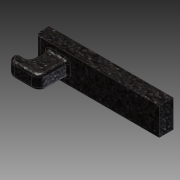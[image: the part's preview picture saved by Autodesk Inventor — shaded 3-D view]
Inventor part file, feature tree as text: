
AUTODESK INVENTOR PART (.ipt)
format: ipt  version: 2012 (Build 160160000, 160)  size: 162,304 bytes
history: native  units: mm
features: fillet x10, extrude x2, sketch x1
ambient origin geometry x8: Origin, YZ Plane, XZ Plane, XY Plane, X Axis, Y Axis, Z Axis, Center Point
bodies: Solid1 (feature_tree)
feature tree (13):
  sketch  "Sketch1"  dims[d0=13.0mm d1=4.0mm d2=8.0mm d3=7.3mm d4=49.5mm d5=5.6mm d6=5.6mm d7=0.0mm d8=3.0mm d9=2.0mm d10=2.0mm d11=3.0mm d12=1.0mm d13=2.0mm d14=1.0mm d15=1.0mm d16=1.0mm d17=11.0mm d18=0.0mm d19=2.0mm]
  extrude  "Extrusion1"  Depth=4.0mm
  extrude  "Extrusion2"  Depth=8.0mm
  fillet  "Fillet1"  Radius=7.3mm
  fillet  "Fillet2"  Radius=49.5mm
  fillet  "Fillet3"  Radius=5.6mm
  fillet  "Fillet4"  Radius=5.6mm
  fillet  "Fillet5"  Radius=3.0mm
  fillet  "Fillet6"  Radius=2.0mm
  fillet  "Fillet7"  Radius=2.0mm
  fillet  "Fillet8"  Radius=3.0mm
  fillet  "Fillet9"  Radius=1.0mm
  fillet  "Fillet10"  Radius=2.0mm
